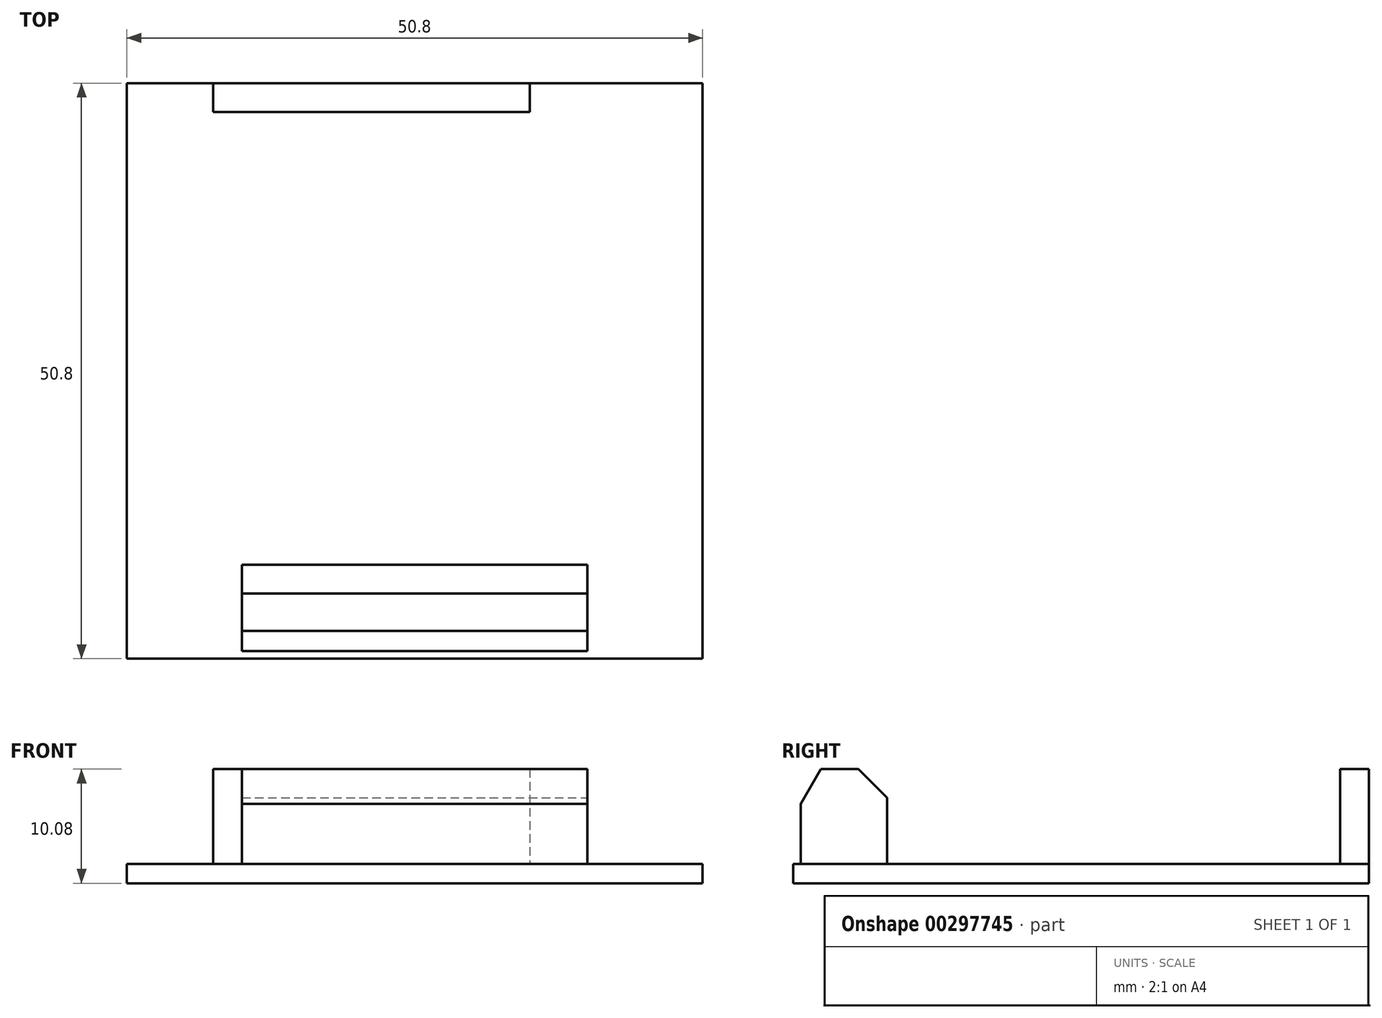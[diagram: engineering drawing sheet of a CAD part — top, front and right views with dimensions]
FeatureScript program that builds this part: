
annotation { "Feature Type Name" : "Feature", "Feature Type Description" : "" }
export const myFeature = defineFeature(function(context is Context, id is Id, definition is map)
    precondition{}
    {
        {
            var Q0;
            Q0=qCreatedBy(makeId("Top.planeOp"),FACE);
            var sketch = newSketch(context, id + "F0", { "sketchPlane" : qUnion([Q0])});
            skLineSegment(sketch, "E0.bottom", {"start": v(-25.4, 25.4) * mm, "end": v(25.4, 25.4) * mm});
            skLineSegment(sketch, "E0.top", {"start": v(-25.4, -25.4) * mm, "end": v(25.4, -25.4) * mm});
            skLineSegment(sketch, "E0.left", {"start": v(-25.4, 25.4) * mm, "end": v(-25.4, -25.4) * mm});
            skLineSegment(sketch, "E0.right", {"start": v(25.4, 25.4) * mm, "end": v(25.4, -25.4) * mm});
            skPoint(sketch, "E0.middle", {"position": v(0, 0) * mm});
            skSolve(sketch);
        }
        {
            var Q0;
            Q0 = qSketchRegion(id + "F0", true);
            extrude(context, id + "F1", {"entities" : qUnion([Q0]), "depth" : 1.7 * mm});
        }
        {
            var Q0;
            Q0=makeQuery(id+"F1.opExtrude","CAP_FACE",FACE,{"disambiguationData":[OSD([sQuery(id+"F0.wireOp",EDGE,"E0.bottom"),sQuery(id+"F0.wireOp",EDGE,"E0.top"),sQuery(id+"F0.wireOp",EDGE,"E0.left"),sQuery(id+"F0.wireOp",EDGE,"E0.right")])],"isStart":false});
            var sketch = newSketch(context, id + "F2", { "sketchPlane" : qUnion([Q0])});
            skLineSegment(sketch, "E1.bottom", {"start": v(-15.24, -17.11) * mm, "end": v(15.24, -17.11) * mm});
            skLineSegment(sketch, "E1.top", {"start": v(-15.24, -24.73) * mm, "end": v(15.24, -24.73) * mm});
            skLineSegment(sketch, "E1.left", {"start": v(-15.24, -17.11) * mm, "end": v(-15.24, -24.73) * mm});
            skLineSegment(sketch, "E1.right", {"start": v(15.24, -17.11) * mm, "end": v(15.24, -24.73) * mm});
            skPoint(sketch, "E1.middle", {"position": v(0, -20.92) * mm});
            skSolve(sketch);
        }
        {
            var Q0;
            Q0 = qSketchRegion(id + "F2", true);
            extrude(context, id + "F3", {"entities" : qUnion([Q0]), "depth" : 8.38 * mm});
        }
        {
            var Q0;
            Q0=makeQuery(id+"F1.opExtrude","CAP_FACE",FACE,{"disambiguationData":[OSD([sQuery(id+"F0.wireOp",EDGE,"E0.bottom"),sQuery(id+"F0.wireOp",EDGE,"E0.top"),sQuery(id+"F0.wireOp",EDGE,"E0.left"),sQuery(id+"F0.wireOp",EDGE,"E0.right")])],"isStart":false});
            var sketch = newSketch(context, id + "F4", { "sketchPlane" : qUnion([Q0])});
            skLineSegment(sketch, "E2.bottom", {"start": v(10.16, 22.86) * mm, "end": v(-17.78, 22.86) * mm});
            skLineSegment(sketch, "E2.top", {"start": v(10.16, 25.4) * mm, "end": v(-17.78, 25.4) * mm});
            skLineSegment(sketch, "E2.left", {"start": v(10.16, 22.86) * mm, "end": v(10.16, 25.4) * mm});
            skLineSegment(sketch, "E2.right", {"start": v(-17.78, 22.86) * mm, "end": v(-17.78, 25.4) * mm});
            skPoint(sketch, "E2.middle", {"position": v(0, 22.69) * mm});
            skSolve(sketch);
        }
        {
            var Q0;
            Q0 = qSketchRegion(id + "F4", true);
            extrude(context, id + "F5", {"entities" : qUnion([Q0]), "depth" : 8.38 * mm});
        }
        {
            var Q0;
            Q0=makeQuery(id+"F3.opExtrude","CAP_EDGE",EDGE,{"disambiguationData":[OSD([sQuery(id+"F2.wireOp",EDGE,"E1.bottom")])],"isStart":false});
            chamfer(context, id + "F6", {"entities" : qUnion([Q0]), "width" : 2.54 * mm, "tangentPropagation" : true});
        }
        {
            var Q0;
            Q0=makeQuery(id+"F3.opExtrude","CAP_EDGE",EDGE,{"disambiguationData":[OSD([sQuery(id+"F2.wireOp",EDGE,"E1.top")])],"isStart":false});
            chamfer(context, id + "F7", {"entities" : qUnion([Q0]), "chamferType" : ChamferType.OFFSET_ANGLE, "width" : 1.78 * mm, "oppositeDirection" : false, "angle" : 60 * degree, "tangentPropagation" : true});
        }
    });
